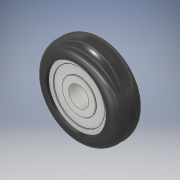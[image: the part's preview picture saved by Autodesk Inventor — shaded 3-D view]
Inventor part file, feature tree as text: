
AUTODESK INVENTOR PART (.ipt)
format: ipt  version: 2019 (Build 230136000, 136)  size: 211,968 bytes
history: native  units: mm
features: extrude x4, sketch x4, other x1, fillet x1, chamfer x1, mirror x1
ambient origin geometry x8: Origin, YZ Plane, XZ Plane, XY Plane, X Axis, Y Axis, Z Axis, Center Point
bodies: Body1 (feature_tree)
feature tree (12):
  other  "Твердое тело1"
  extrude  "Выдавливание1"  Depth=21.5mm
  fillet  "Сопряжение1"  Radius=7.2mm
  extrude  "Выдавливание2"  Depth=2.8mm
  extrude  "Выдавливание3"  Depth=15.0mm
  extrude  "Выдавливание4"  Depth=0.8mm TaperAngle=0.0deg
  chamfer  "Фаска1"  Distance=8.5mm
  mirror  "Зеркальное отражение2"
  sketch  "Эскиз1"
  sketch  "Эскиз2"
  sketch  "Эскиз3"
  sketch  "Эскиз4"
